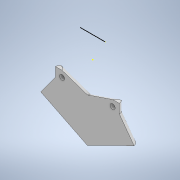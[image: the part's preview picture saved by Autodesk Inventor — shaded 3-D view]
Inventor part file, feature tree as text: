
AUTODESK INVENTOR PART (.ipt)
format: ipt  version: 2022 (Build 260153000, 153)  size: 306,176 bytes
history: native  units: in
note: dims shown in document units (in); Inventor stores cm internally (conversion verified against a paired STEP export)
features: extrude x5, sketch x5, fillet x2, projected_geometry x1
ambient origin geometry x8: Origin, YZ Plane, XZ Plane, XY Plane, X Axis, Y Axis, Z Axis, Center Point
bodies: Solid1 (feature_tree)
feature tree (13):
  extrude  "Extrusion1"  Depth=5.0in
  extrude  "Extrusion2"  Depth=0.12in
  fillet  "Fillet1"  Radius=0.12in
  extrude  "Extrusion3"  Depth=0.25in
  sketch  "Sketch5"  dims[d7=0.25in d8=0.25in]
  sketch  "Sketch6"  dims[d9=0.125in d10=0.0in d11=0.3in d12=0.12in d13=0.12in d14=0.12in d15=0.12in d16=1.22in d19=1.0in d20=0.0in d21=1.22in d22=1.22in d23=0.125in d24=2.0in d25=0.5in d26=0.2953in d27=0.2953in d28=0.0738in d29=0.0738in d30=0.0394in d31=0.0in d32=0.0in d33=0.0in d36=0.0394in d37=0.0in d38=0.125in]
  extrude  "Extrusion4"  Depth=0.25in
  extrude  "Extrusion6"  Depth=0.125in
  fillet  "Fillet2"  Radius=0.12in
  sketch  "Sketch1"  dims[d0=5.0in d1=5.0in]
  sketch  "Sketch2"  dims[d2=5.0in d3=0.12in d4=0.12in]
  sketch  "Sketch4"  dims[d5=0.25in d6=0.25in]
  projected_geometry  "Projected Loop1"
